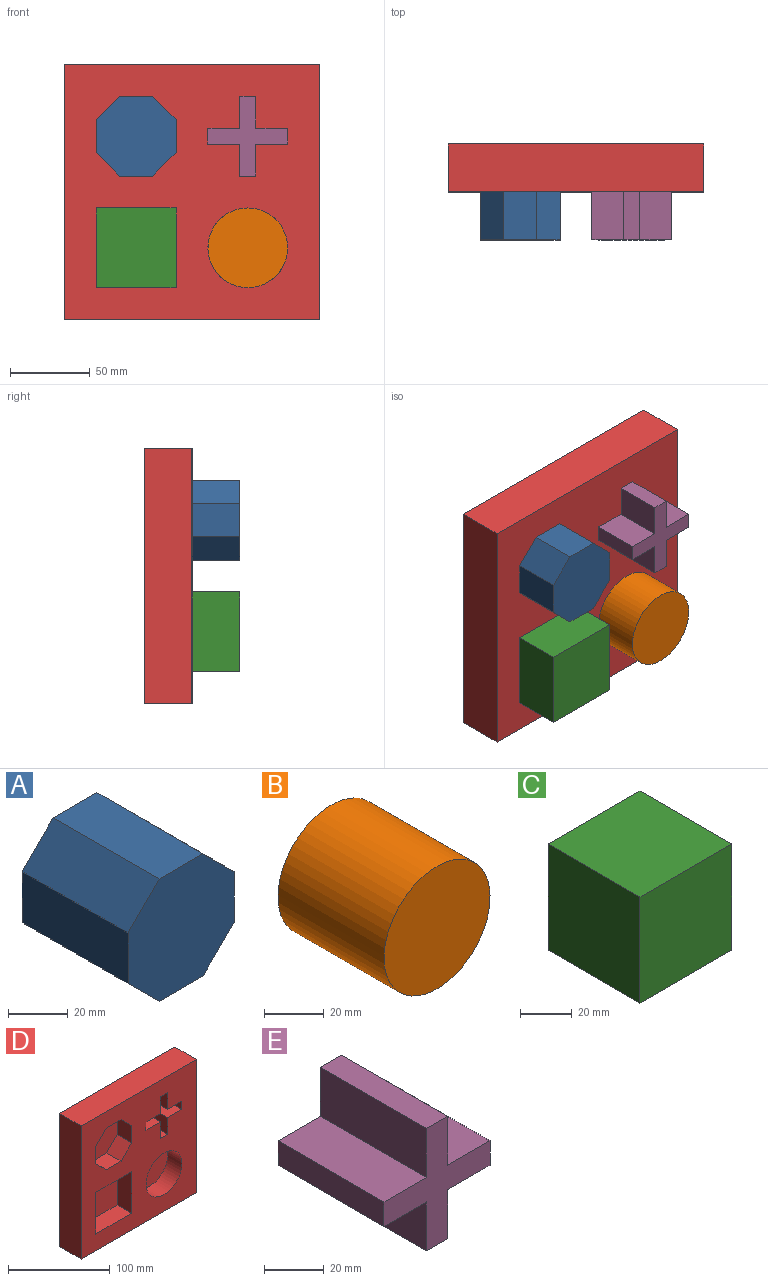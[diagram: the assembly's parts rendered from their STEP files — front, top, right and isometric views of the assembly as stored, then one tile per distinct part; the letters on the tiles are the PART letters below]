
ASSEMBLY  parts=5 mates=4
PART A: 10 faces, bbox 50x50x50 mm
  f0: plane 50x14.64mm, normal (0.71,0,-0.71), area 1035.5mm2, adj f1,f7,f8,f9
  f1: plane 50x20.71mm, normal (1,0,0), area 1035.5mm2, adj f0,f2,f8,f9
  f2: plane 50x14.64mm, normal (0.71,0,0.71), area 1035.5mm2, adj f1,f3,f8,f9
  f3: plane 50x20.71mm, normal (0,0,1), area 1035.5mm2, adj f2,f4,f8,f9
  f4: plane 50x14.64mm, normal (-0.71,0,0.71), area 1035.5mm2, adj f3,f5,f8,f9
  f5: plane 50x20.71mm, normal (-1,0,0), area 1035.5mm2, adj f4,f6,f8,f9
  f6: plane 50x14.64mm, normal (-0.71,0,-0.71), area 1035.5mm2, adj f5,f7,f8,f9
  f7: plane 50x20.71mm, normal (0,0,-1), area 1035.5mm2, adj f0,f6,f8,f9
  f8: plane 50x50mm, normal (0,-1,0), area 2071.1mm2, adj f0,f1,f2,f3,f4,f5,f6,f7
  f9: plane 50x50mm, normal (0,1,0), area 2071.1mm2, adj f0,f1,f2,f3,f4,f5,f6,f7
PART B: 3 faces, bbox 50x50x50 mm
  f0: cylinder r=25mm len=50mm, axis (0,1,0), area 7854mm2, adj f1,f2
  f1: plane 50x50mm, normal (0,-1,0), area 1963.5mm2, adj f0
  f2: plane 50x50mm, normal (0,1,0), area 1963.5mm2, adj f0
PART C: 6 faces, bbox 50x50x50 mm
  f0: plane 50x50mm, normal (1,0,0), area 2500mm2, adj f1,f3,f4,f5
  f1: plane 50x50mm, normal (0,0,1), area 2500mm2, adj f0,f2,f4,f5
  f2: plane 50x50mm, normal (-1,0,0), area 2500mm2, adj f1,f3,f4,f5
  f3: plane 50x50mm, normal (0,0,-1), area 2500mm2, adj f0,f2,f4,f5
  f4: plane 50x50mm, normal (0,-1,0), area 2500mm2, adj f0,f1,f2,f3
  f5: plane 50x50mm, normal (0,1,0), area 2500mm2, adj f0,f1,f2,f3
PART D: 35 faces, bbox 160x30x160 mm
  f0: plane 160x30mm, normal (1,0,0), area 4800mm2, adj f1,f3,f4,f30
  f1: plane 160x30mm, normal (0,0,1), area 4800mm2, adj f0,f2,f4,f30
  f2: plane 160x30mm, normal (-1,0,0), area 4800mm2, adj f1,f3,f4,f30
  f3: plane 160x30mm, normal (0,0,-1), area 4800mm2, adj f0,f2,f4,f30
  f4: plane 160x160mm, normal (0,1,0), area 25600mm2, adj f0,f1,f2,f3
  f5: plane 50x20mm, normal (0,0,-1), area 1000mm2, adj f6,f29,f30,f31
  f6: plane 50x20mm, normal (-1,0,0), area 1000mm2, adj f5,f7,f30,f31
  f7: plane 50x20mm, normal (0,0,1), area 1000mm2, adj f6,f29,f30,f31
  f8: plane 20x10mm, normal (0,0,1), area 200mm2, adj f9,f26,f30,f32
  f9: plane 20x20mm, normal (1,0,0), area 400mm2, adj f8,f10,f30,f32
  f10: plane 20x20mm, normal (0,0,1), area 400mm2, adj f9,f11,f30,f32
  f11: plane 20x10mm, normal (1,0,0), area 200mm2, adj f10,f12,f30,f32
  f12: plane 20x20mm, normal (0,0,-1), area 400mm2, adj f11,f13,f30,f32
  f13: plane 20x20mm, normal (1,0,0), area 400mm2, adj f12,f14,f30,f32
  f14: plane 20x10mm, normal (0,0,-1), area 200mm2, adj f13,f15,f30,f32
  f15: plane 20.22x20mm, normal (-1,0,0), area 404.4mm2, adj f14,f16,f30,f32
  f16: plane 20x20mm, normal (0.01,0,-1), area 400mm2, adj f15,f17,f30,f32
  f17: plane 20x10mm, normal (-1,0,0), area 200mm2, adj f16,f18,f30,f32
  f18: plane 20x20mm, normal (0,0,1), area 400mm2, adj f17,f26,f30,f32
  f19: plane 20x14.64mm, normal (-0.71,0,-0.71), area 414.2mm2, adj f20,f28,f30,f34
  f20: plane 20.71x20mm, normal (-1,0,0), area 414.2mm2, adj f19,f21,f30,f34
  f21: plane 20x14.64mm, normal (-0.71,0,0.71), area 414.2mm2, adj f20,f22,f30,f34
  f22: plane 20.71x20mm, normal (0,0,1), area 414.2mm2, adj f21,f23,f30,f34
  f23: plane 20x14.64mm, normal (0.71,0,0.71), area 414.2mm2, adj f22,f24,f30,f34
  f24: plane 20.71x20mm, normal (1,0,0), area 414.2mm2, adj f23,f25,f30,f34
  f25: plane 20x14.64mm, normal (0.71,0,-0.71), area 414.2mm2, adj f24,f28,f30,f34
  f26: plane 20x20mm, normal (-1,0,0), area 400mm2, adj f8,f18,f30,f32
  f27: cylinder r=25mm len=50mm, axis (0,1,0), area 3141.6mm2, adj f30,f33
  f28: plane 20.71x20mm, normal (0,0,-1), area 414.2mm2, adj f19,f25,f30,f34
  f29: plane 50x20mm, normal (1,0,0), area 1000mm2, adj f5,f7,f30,f31
  f30: plane 160x160mm, normal (0,-1,0), area 18167.7mm2, adj f0,f1,f2,f3,f5,f6,f7,f8
  f31: plane 50x50mm, normal (0,-1,0), area 2500mm2, adj f5,f6,f7,f29
  f32: plane 50x50mm, normal (0,-1,0), area 897.8mm2, adj f8,f9,f10,f11,f12,f13,f14,f15
  f33: plane 50x50mm, normal (0,-1,0), area 1963.5mm2, adj f27
  f34: plane 50x50mm, normal (0,-1,0), area 2071.1mm2, adj f19,f20,f21,f22,f23,f24,f25,f28
PART E: 14 faces, bbox 50x50x50 mm
  f0: plane 50x10mm, normal (0,0,-1), area 500mm2, adj f1,f11,f12,f13
  f1: plane 50x20mm, normal (1,0,0), area 1000mm2, adj f0,f2,f12,f13
  f2: plane 50x20mm, normal (0,0,-1), area 1000mm2, adj f1,f3,f12,f13
  f3: plane 50x10mm, normal (1,0,0), area 500mm2, adj f2,f4,f12,f13
  f4: plane 50x20mm, normal (0,0,1), area 1000mm2, adj f3,f5,f12,f13
  f5: plane 50x20mm, normal (1,0,0), area 1000mm2, adj f4,f6,f12,f13
  f6: plane 50x10mm, normal (0,0,1), area 500mm2, adj f5,f7,f12,f13
  f7: plane 50x20mm, normal (-1,0,0), area 1000mm2, adj f6,f8,f12,f13
  f8: plane 50x20mm, normal (0,0,1), area 1000mm2, adj f7,f9,f12,f13
  f9: plane 50x10mm, normal (-1,0,0), area 500mm2, adj f8,f10,f12,f13
  f10: plane 50x20mm, normal (0,0,-1), area 1000mm2, adj f9,f11,f12,f13
  f11: plane 50x20mm, normal (-1,0,0), area 1000mm2, adj f0,f10,f12,f13
  f12: plane 50x50mm, normal (0,-1,0), area 900mm2, adj f0,f1,f2,f3,f4,f5,f6,f7
  f13: plane 50x50mm, normal (0,1,0), area 900mm2, adj f0,f1,f2,f3,f4,f5,f6,f7
PLACE A rot(axis=(1,0,0),180deg) t=(-84.6,-73.48,-14.04)mm
PLACE B rot(axis=(1,0,0),180deg) t=(-14.6,-73.48,-34.77)mm
PLACE C rot(axis=(-1,0,0),90deg) t=(-84.6,-48.48,-59.77)mm
PLACE D t=(-49.6,-23.48,0.23)mm fixed
PLACE E t=(-14.62,-23.48,35.22)mm
MATE fastened A.f8 <-> D.f34  axis (0,1,0) through (-84.6,-23.48,35.23)mm
MATE fastened E.f13 <-> D.f32  axis (0,1,0) through (-14.62,-23.48,35.22)mm
MATE fastened B.f0 <-> D.f27  axis (0,1,0) through (-14.6,-23.48,-34.77)mm
MATE fastened C.f1 <-> D.f31  axis (0,1,0) through (-84.6,-23.48,-34.77)mm
